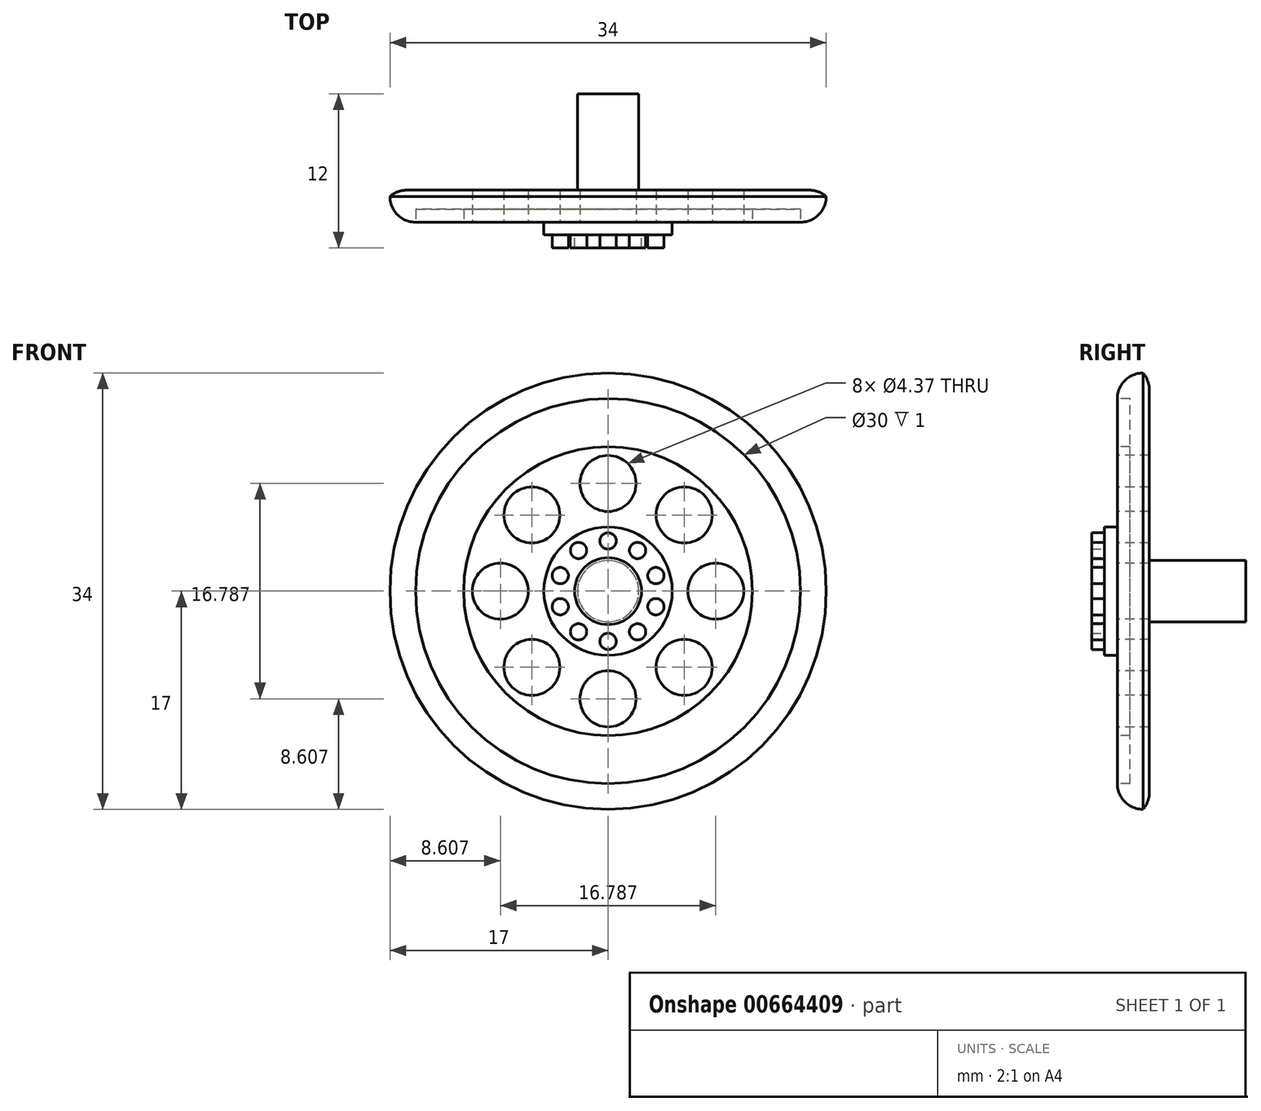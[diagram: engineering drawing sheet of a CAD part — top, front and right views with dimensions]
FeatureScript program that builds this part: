
annotation { "Feature Type Name" : "Feature", "Feature Type Description" : "" }
export const myFeature = defineFeature(function(context is Context, id is Id, definition is map)
    precondition{}
    {
        {
            var Q0;
            Q0=qCreatedBy(makeId("Front.planeOp"),FACE);
            var sketch = newSketch(context, id + "F0", { "sketchPlane" : qUnion([Q0])});
            skCircle(sketch, "E0", {"center": v(0, 0) * mm, "radius": 17 * mm});
            skSolve(sketch);
        }
        {
            var Q0;
            Q0=makeQuery(id+"F0.imprint","IMPRINT",FACE,{"disambiguationData":[TD([[makeQuery(id+"F0.imprint","IMPRINT",EDGE,{"derivedFrom":sQuery(id+"F0.wireOp",EDGE,"E0")}),1.0]])]});
            extrude(context, id + "F1", {"entities" : qUnion([Q0]), "depth" : 2.5 * mm, "offsetDistance" : 25.4 * mm});
        }
        {
            var Q0;
            Q0=makeQuery(id+"F1.opExtrude","CAP_EDGE",EDGE,{"disambiguationData":[OSD([sQuery(id+"F0.wireOp",EDGE,"E0")])],"isStart":false});
            fillet(context, id + "F2", {"entities" : qUnion([Q0]), "radius" : 2 * mm, "tangentPropagation" : true, "allowEdgeOverflow" : false});
        }
        {
            var Q0;
            Q0=makeQuery(id+"F1.opExtrude","CAP_EDGE",EDGE,{"disambiguationData":[OSD([sQuery(id+"F0.wireOp",EDGE,"E0")])],"isStart":true});
            fillet(context, id + "F3", {"entities" : qUnion([Q0]), "radius" : 2 * mm, "tangentPropagation" : true, "allowEdgeOverflow" : false});
        }
        {
            var Q0;
            Q0=makeQuery(id+"F1.opExtrude","CAP_FACE",FACE,{"disambiguationData":[OSD([sQuery(id+"F0.wireOp",EDGE,"E0")])],"isStart":false});
            var sketch = newSketch(context, id + "F4", { "sketchPlane" : qUnion([Q0])});
            skCircle(sketch, "E1", {"center": v(0, 0) * mm, "radius": 11.25 * mm});
            skSolve(sketch);
        }
        {
            var Q0;
            Q0=makeQuery(id+"F4.imprint","IMPRINT",FACE,{"disambiguationData":[TD([[makeQuery(id+"F4.imprint","IMPRINT",EDGE,{"derivedFrom":sQuery(id+"F4.wireOp",EDGE,"E1")}),1.0]])]});
            var sketch = newSketch(context, id + "F5", { "sketchPlane" : qUnion([Q0])});
            skCircle(sketch, "E2", {"center": v(0, 0) * mm, "radius": 5 * mm});
            skSolve(sketch);
        }
        {
            var Q0;
            Q0=makeQuery(id+"F4.imprint","IMPRINT",FACE,{"disambiguationData":[TD([[makeQuery(id+"F4.imprint","IMPRINT",EDGE,{"derivedFrom":sQuery(id+"F4.wireOp",EDGE,"E1")}),-1.0]])]});
            extrude(context, id + "F6", {"entities" : qUnion([Q0]), "operationType" : NewBodyOperationType.REMOVE, "oppositeDirection" : true, "depth" : 1 * mm, "offsetDistance" : 25.4 * mm});
        }
        {
            var Q0;
            Q0=makeQuery(id+"F5.imprint","IMPRINT",FACE,{"disambiguationData":[TD([[makeQuery(id+"F5.imprint","IMPRINT",EDGE,{"derivedFrom":sQuery(id+"F5.wireOp",EDGE,"E2")}),-1.0]])]});
            var sketch = newSketch(context, id + "F7", { "sketchPlane" : qUnion([Q0])});
            skCircle(sketch, "E3", {"center": v(0, 8.4) * mm, "radius": 2.19 * mm});
            skCircle(sketch, "E4.1.0", {"center": v(-5.94, 5.94) * mm, "radius": 2.19 * mm});
            skCircle(sketch, "E4.2.0", {"center": v(-8.4, 0) * mm, "radius": 2.19 * mm});
            skCircle(sketch, "E4.3.0", {"center": v(-5.94, -5.94) * mm, "radius": 2.19 * mm});
            skCircle(sketch, "E4.4.0", {"center": v(0, -8.4) * mm, "radius": 2.19 * mm});
            skCircle(sketch, "E4.5.0", {"center": v(5.94, -5.94) * mm, "radius": 2.19 * mm});
            skCircle(sketch, "E4.6.0", {"center": v(8.4, 0) * mm, "radius": 2.19 * mm});
            skCircle(sketch, "E4.7.0", {"center": v(5.94, 5.94) * mm, "radius": 2.19 * mm});
            skPoint(sketch, "E4.center", {"position": v(0, 0) * mm});
            skSolve(sketch);
        }
        {
            var Q0;
            Q0=makeQuery(id+"F5.imprint","IMPRINT",FACE,{"disambiguationData":[TD([[makeQuery(id+"F5.imprint","IMPRINT",EDGE,{"derivedFrom":sQuery(id+"F5.wireOp",EDGE,"E2")}),1.0]])]});
            extrude(context, id + "F8", {"entities" : qUnion([Q0]), "operationType" : NewBodyOperationType.ADD, "depth" : 1 * mm, "offsetDistance" : 25.4 * mm});
        }
        {
            var Q0;
            Q0=makeQuery(id+"F7.imprint","IMPRINT",FACE,{"disambiguationData":[TD([[makeQuery(id+"F7.imprint","IMPRINT",EDGE,{"derivedFrom":sQuery(id+"F7.wireOp",EDGE,"E3")}),1.0]])]});
            var Q1;
            Q1=makeQuery(id+"F7.imprint","IMPRINT",FACE,{"disambiguationData":[TD([[makeQuery(id+"F7.imprint","IMPRINT",EDGE,{"derivedFrom":sQuery(id+"F7.wireOp",EDGE,"E4.7.0")}),1.0]])]});
            var Q2;
            Q2=makeQuery(id+"F7.imprint","IMPRINT",FACE,{"disambiguationData":[TD([[makeQuery(id+"F7.imprint","IMPRINT",EDGE,{"derivedFrom":sQuery(id+"F7.wireOp",EDGE,"E4.6.0")}),1.0]])]});
            var Q3;
            Q3=makeQuery(id+"F7.imprint","IMPRINT",FACE,{"disambiguationData":[TD([[makeQuery(id+"F7.imprint","IMPRINT",EDGE,{"derivedFrom":sQuery(id+"F7.wireOp",EDGE,"E4.5.0")}),1.0]])]});
            var Q4;
            Q4=makeQuery(id+"F7.imprint","IMPRINT",FACE,{"disambiguationData":[TD([[makeQuery(id+"F7.imprint","IMPRINT",EDGE,{"derivedFrom":sQuery(id+"F7.wireOp",EDGE,"E4.4.0")}),1.0]])]});
            var Q5;
            Q5=makeQuery(id+"F7.imprint","IMPRINT",FACE,{"disambiguationData":[TD([[makeQuery(id+"F7.imprint","IMPRINT",EDGE,{"derivedFrom":sQuery(id+"F7.wireOp",EDGE,"E4.3.0")}),1.0]])]});
            var Q6;
            Q6=makeQuery(id+"F7.imprint","IMPRINT",FACE,{"disambiguationData":[TD([[makeQuery(id+"F7.imprint","IMPRINT",EDGE,{"derivedFrom":sQuery(id+"F7.wireOp",EDGE,"E4.2.0")}),1.0]])]});
            var Q7;
            Q7=makeQuery(id+"F7.imprint","IMPRINT",FACE,{"disambiguationData":[TD([[makeQuery(id+"F7.imprint","IMPRINT",EDGE,{"derivedFrom":sQuery(id+"F7.wireOp",EDGE,"E4.1.0")}),1.0]])]});
            extrude(context, id + "F9", {"entities" : qUnion([Q0, Q1, Q2, Q3, Q4, Q5, Q6, Q7]), "operationType" : NewBodyOperationType.REMOVE, "oppositeDirection" : true, "depth" : 25.4 * mm, "offsetDistance" : 25.4 * mm});
        }
        {
            var Q0;
            Q0=makeQuery(id+"F8.opExtrude","CAP_FACE",FACE,{"disambiguationData":[OSD([sQuery(id+"F5.wireOp",EDGE,"E2")])],"isStart":false});
            var sketch = newSketch(context, id + "F10", { "sketchPlane" : qUnion([Q0])});
            skCircle(sketch, "E5", {"center": v(0, 0) * mm, "radius": 2.6 * mm});
            skSolve(sketch);
        }
        {
            var Q0;
            Q0=makeQuery(id+"F10.imprint","IMPRINT",FACE,{"disambiguationData":[TD([[makeQuery(id+"F10.imprint","IMPRINT",EDGE,{"derivedFrom":sQuery(id+"F10.wireOp",EDGE,"E5")}),1.0]])]});
            extrude(context, id + "F11", {"entities" : qUnion([Q0]), "operationType" : NewBodyOperationType.ADD, "depth" : 1 * mm, "offsetDistance" : 25.4 * mm});
        }
        {
            var Q0;
            Q0=makeQuery(id+"F8.opExtrude","CAP_FACE",FACE,{"disambiguationData":[OSD([sQuery(id+"F5.wireOp",EDGE,"E2")])],"isStart":false});
            var sketch = newSketch(context, id + "F12", { "sketchPlane" : qUnion([Q0])});
            skCircle(sketch, "E6", {"center": v(0, 3.92) * mm, "radius": 0.64 * mm});
            skCircle(sketch, "E7.1.0", {"center": v(-2.3, 3.17) * mm, "radius": 0.64 * mm});
            skCircle(sketch, "E7.2.0", {"center": v(-3.72, 1.2) * mm, "radius": 0.64 * mm});
            skCircle(sketch, "E7.3.0", {"center": v(-3.72, -1.2) * mm, "radius": 0.64 * mm});
            skCircle(sketch, "E7.4.0", {"center": v(-2.3, -3.17) * mm, "radius": 0.64 * mm});
            skCircle(sketch, "E7.5.0", {"center": v(0, -3.92) * mm, "radius": 0.64 * mm});
            skCircle(sketch, "E7.6.0", {"center": v(2.3, -3.17) * mm, "radius": 0.64 * mm});
            skCircle(sketch, "E7.7.0", {"center": v(3.72, -1.2) * mm, "radius": 0.64 * mm});
            skCircle(sketch, "E7.8.0", {"center": v(3.72, 1.2) * mm, "radius": 0.64 * mm});
            skCircle(sketch, "E7.9.0", {"center": v(2.3, 3.17) * mm, "radius": 0.64 * mm});
            skPoint(sketch, "E7.center", {"position": v(0, 0) * mm});
            skSolve(sketch);
        }
        {
            var Q0;
            Q0=makeQuery(id+"F12.imprint","IMPRINT",FACE,{"disambiguationData":[TD([[makeQuery(id+"F12.imprint","IMPRINT",EDGE,{"derivedFrom":sQuery(id+"F12.wireOp",EDGE,"E7.1.0")}),1.0]])]});
            var Q1;
            Q1=makeQuery(id+"F12.imprint","IMPRINT",FACE,{"disambiguationData":[TD([[makeQuery(id+"F12.imprint","IMPRINT",EDGE,{"derivedFrom":sQuery(id+"F12.wireOp",EDGE,"E6")}),1.0]])]});
            var Q2;
            Q2=makeQuery(id+"F12.imprint","IMPRINT",FACE,{"disambiguationData":[TD([[makeQuery(id+"F12.imprint","IMPRINT",EDGE,{"derivedFrom":sQuery(id+"F12.wireOp",EDGE,"E7.9.0")}),1.0]])]});
            var Q3;
            Q3=makeQuery(id+"F12.imprint","IMPRINT",FACE,{"disambiguationData":[TD([[makeQuery(id+"F12.imprint","IMPRINT",EDGE,{"derivedFrom":sQuery(id+"F12.wireOp",EDGE,"E7.8.0")}),1.0]])]});
            var Q4;
            Q4=makeQuery(id+"F12.imprint","IMPRINT",FACE,{"disambiguationData":[TD([[makeQuery(id+"F12.imprint","IMPRINT",EDGE,{"derivedFrom":sQuery(id+"F12.wireOp",EDGE,"E7.7.0")}),1.0]])]});
            var Q5;
            Q5=makeQuery(id+"F12.imprint","IMPRINT",FACE,{"disambiguationData":[TD([[makeQuery(id+"F12.imprint","IMPRINT",EDGE,{"derivedFrom":sQuery(id+"F12.wireOp",EDGE,"E7.6.0")}),1.0]])]});
            var Q6;
            Q6=makeQuery(id+"F12.imprint","IMPRINT",FACE,{"disambiguationData":[TD([[makeQuery(id+"F12.imprint","IMPRINT",EDGE,{"derivedFrom":sQuery(id+"F12.wireOp",EDGE,"E7.5.0")}),1.0]])]});
            var Q7;
            Q7=makeQuery(id+"F12.imprint","IMPRINT",FACE,{"disambiguationData":[TD([[makeQuery(id+"F12.imprint","IMPRINT",EDGE,{"derivedFrom":sQuery(id+"F12.wireOp",EDGE,"E7.4.0")}),1.0]])]});
            var Q8;
            Q8=makeQuery(id+"F12.imprint","IMPRINT",FACE,{"disambiguationData":[TD([[makeQuery(id+"F12.imprint","IMPRINT",EDGE,{"derivedFrom":sQuery(id+"F12.wireOp",EDGE,"E7.3.0")}),1.0]])]});
            var Q9;
            Q9=makeQuery(id+"F12.imprint","IMPRINT",FACE,{"disambiguationData":[TD([[makeQuery(id+"F12.imprint","IMPRINT",EDGE,{"derivedFrom":sQuery(id+"F12.wireOp",EDGE,"E7.2.0")}),1.0]])]});
            extrude(context, id + "F13", {"entities" : qUnion([Q0, Q1, Q2, Q3, Q4, Q5, Q6, Q7, Q8, Q9]), "operationType" : NewBodyOperationType.ADD, "depth" : 0.5 * mm, "offsetDistance" : 25.4 * mm});
        }
        {
            var Q0;
            Q0=makeQuery(id+"F13.opExtrude","CAP_FACE",FACE,{"disambiguationData":[OSD([sQuery(id+"F12.wireOp",EDGE,"E7.8.0")])],"isStart":false});
            var Q1;
            Q1=makeQuery(id+"F13.opExtrude","CAP_FACE",FACE,{"disambiguationData":[OSD([sQuery(id+"F12.wireOp",EDGE,"E7.9.0")])],"isStart":false});
            var Q2;
            Q2=makeQuery(id+"F13.opExtrude","CAP_FACE",FACE,{"disambiguationData":[OSD([sQuery(id+"F12.wireOp",EDGE,"E6")])],"isStart":false});
            var Q3;
            Q3=makeQuery(id+"F13.opExtrude","CAP_FACE",FACE,{"disambiguationData":[OSD([sQuery(id+"F12.wireOp",EDGE,"E7.1.0")])],"isStart":false});
            var Q4;
            Q4=makeQuery(id+"F13.opExtrude","CAP_FACE",FACE,{"disambiguationData":[OSD([sQuery(id+"F12.wireOp",EDGE,"E7.2.0")])],"isStart":false});
            var Q5;
            Q5=makeQuery(id+"F13.opExtrude","CAP_FACE",FACE,{"disambiguationData":[OSD([sQuery(id+"F12.wireOp",EDGE,"E7.3.0")])],"isStart":false});
            var Q6;
            Q6=makeQuery(id+"F13.opExtrude","CAP_FACE",FACE,{"disambiguationData":[OSD([sQuery(id+"F12.wireOp",EDGE,"E7.4.0")])],"isStart":false});
            var Q7;
            Q7=makeQuery(id+"F13.opExtrude","CAP_FACE",FACE,{"disambiguationData":[OSD([sQuery(id+"F12.wireOp",EDGE,"E7.5.0")])],"isStart":false});
            var Q8;
            Q8=makeQuery(id+"F13.opExtrude","CAP_FACE",FACE,{"disambiguationData":[OSD([sQuery(id+"F12.wireOp",EDGE,"E7.6.0")])],"isStart":false});
            var Q9;
            Q9=makeQuery(id+"F13.opExtrude","CAP_FACE",FACE,{"disambiguationData":[OSD([sQuery(id+"F12.wireOp",EDGE,"E7.7.0")])],"isStart":false});
            extrude(context, id + "F14", {"entities" : qUnion([Q0, Q1, Q2, Q3, Q4, Q5, Q6, Q7, Q8, Q9]), "operationType" : NewBodyOperationType.ADD, "depth" : 0.5 * mm, "offsetDistance" : 25.4 * mm});
        }
        {
            var Q0;
            Q0=makeQuery(id+"F1.opExtrude","CAP_FACE",FACE,{"disambiguationData":[OSD([sQuery(id+"F0.wireOp",EDGE,"E0")])],"isStart":true});
            var sketch = newSketch(context, id + "F15", { "sketchPlane" : qUnion([Q0])});
            skCircle(sketch, "E8", {"center": v(0, 0) * mm, "radius": 2.39 * mm});
            skSolve(sketch);
        }
        {
            var Q0;
            Q0=makeQuery(id+"F15.imprint","IMPRINT",FACE,{"disambiguationData":[TD([[makeQuery(id+"F15.imprint","IMPRINT",EDGE,{"derivedFrom":sQuery(id+"F15.wireOp",EDGE,"E8")}),1.0]])]});
            extrude(context, id + "F16", {"entities" : qUnion([Q0]), "operationType" : NewBodyOperationType.ADD, "depth" : 7.5 * mm, "offsetDistance" : 25.4 * mm});
        }
    });
